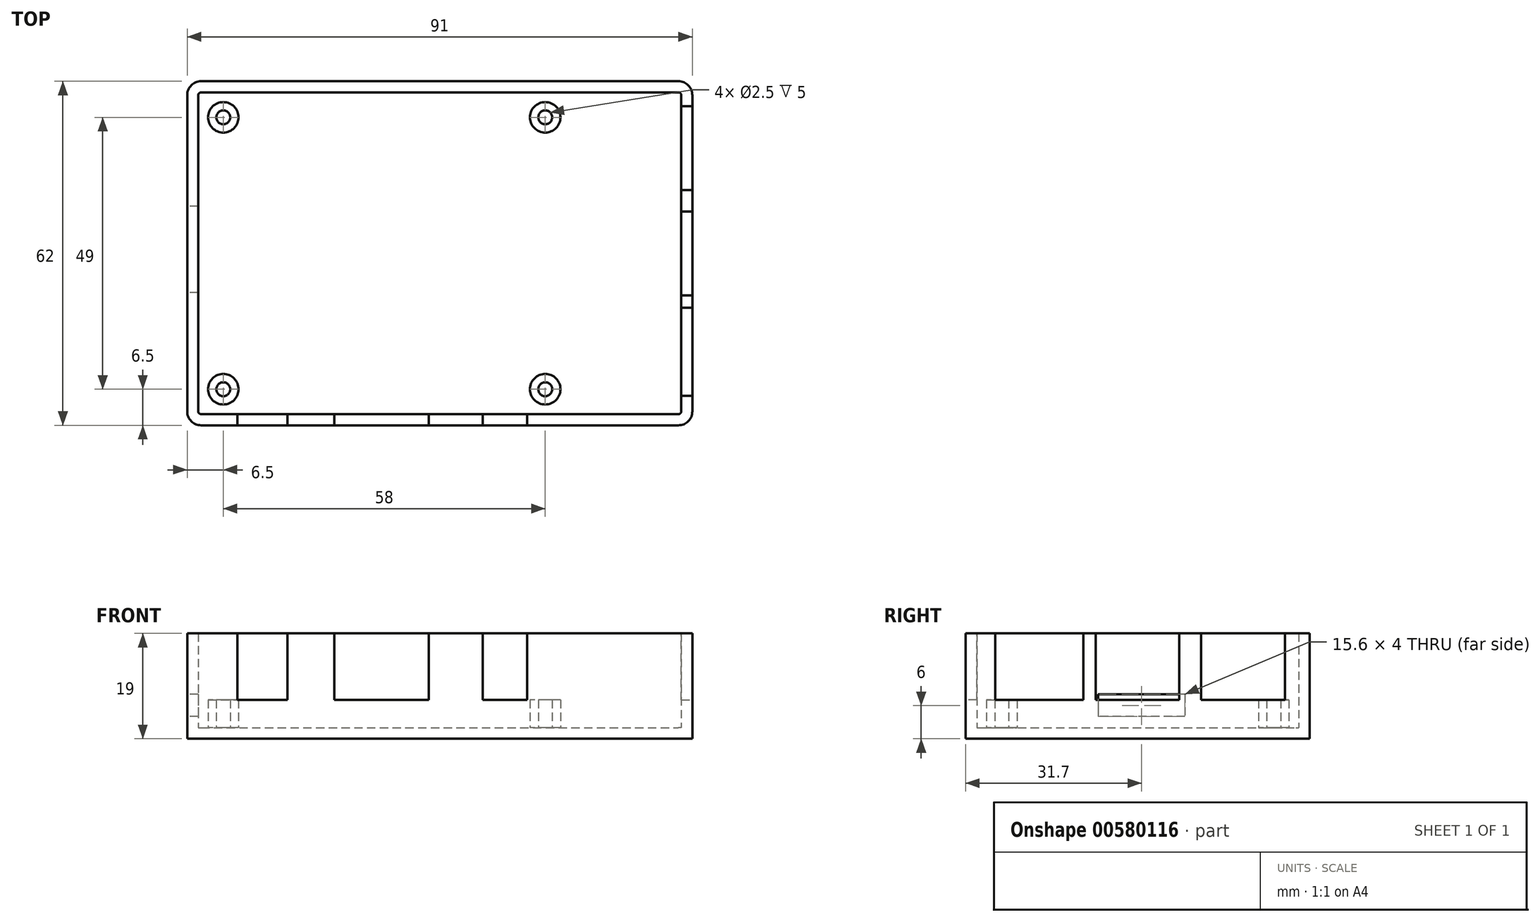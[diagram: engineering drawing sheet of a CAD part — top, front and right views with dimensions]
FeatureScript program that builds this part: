
annotation { "Feature Type Name" : "Feature", "Feature Type Description" : "" }
export const myFeature = defineFeature(function(context is Context, id is Id, definition is map)
    precondition{}
    {
        {
            var Q0;
            Q0=qCreatedBy(makeId("Top.planeOp"),FACE);
            var sketch = newSketch(context, id + "F0", { "sketchPlane" : qUnion([Q0])});
            skLineSegment(sketch, "E0.bottom", {"start": v(43, 31) * mm, "end": v(-43, 31) * mm});
            skLineSegment(sketch, "E0.top", {"start": v(43, -31) * mm, "end": v(-43, -31) * mm});
            skLineSegment(sketch, "E0.left", {"start": v(45.5, 28.5) * mm, "end": v(45.5, -28.5) * mm});
            skLineSegment(sketch, "E0.right", {"start": v(-45.5, 28.5) * mm, "end": v(-45.5, -28.5) * mm});
            skPoint(sketch, "E0.middle", {"position": v(0, 0) * mm});
            skPoint(sketch, "E1.visualSharp", {"position": v(-45.5, 31) * mm});
            skArc(sketch, "E1.filletArc", {"start": v(-43, 31) * mm, "mid": v(-44.77, 30.27) * mm, "end": v(-45.5, 28.5) * mm});
            skPoint(sketch, "E2.visualSharp", {"position": v(45.5, 31) * mm});
            skArc(sketch, "E2.filletArc", {"start": v(45.5, 28.5) * mm, "mid": v(44.77, 30.27) * mm, "end": v(43, 31) * mm});
            skPoint(sketch, "E3.visualSharp", {"position": v(45.5, -31) * mm});
            skArc(sketch, "E3.filletArc", {"start": v(43, -31) * mm, "mid": v(44.77, -30.27) * mm, "end": v(45.5, -28.5) * mm});
            skPoint(sketch, "E4.visualSharp", {"position": v(-45.5, -31) * mm});
            skArc(sketch, "E4.filletArc", {"start": v(-45.5, -28.5) * mm, "mid": v(-44.77, -30.27) * mm, "end": v(-43, -31) * mm});
            skArc(sketch, "E5.0", {"start": v(43.5, 28.5) * mm, "mid": v(43.35, 28.85) * mm, "end": v(43, 29) * mm});
            skLineSegment(sketch, "E5.1", {"start": v(43.5, 28.5) * mm, "end": v(43.5, -28.5) * mm});
            skLineSegment(sketch, "E5.2", {"start": v(43, 29) * mm, "end": v(-43, 29) * mm});
            skArc(sketch, "E5.3", {"start": v(43, -29) * mm, "mid": v(43.35, -28.85) * mm, "end": v(43.5, -28.5) * mm});
            skArc(sketch, "E5.4", {"start": v(-43, 29) * mm, "mid": v(-43.35, 28.85) * mm, "end": v(-43.5, 28.5) * mm});
            skLineSegment(sketch, "E5.5", {"start": v(-43.5, 28.5) * mm, "end": v(-43.5, -28.5) * mm});
            skArc(sketch, "E5.6", {"start": v(-43.5, -28.5) * mm, "mid": v(-43.35, -28.85) * mm, "end": v(-43, -29) * mm});
            skLineSegment(sketch, "E5.7", {"start": v(43, -29) * mm, "end": v(-43, -29) * mm});
            skSolve(sketch);
        }
        {
            var Q0;
            Q0=makeQuery(id+"F0.imprint","IMPRINT",FACE,{"disambiguationData":[TD([[makeQuery(id+"F0.imprint","IMPRINT",EDGE,{"derivedFrom":sQuery(id+"F0.wireOp",EDGE,"E0.bottom")}),1.0]])]});
            var Q1;
            Q1=makeQuery(id+"F0.imprint","IMPRINT",FACE,{"disambiguationData":[TD([[makeQuery(id+"F0.imprint","IMPRINT",EDGE,{"derivedFrom":sQuery(id+"F0.wireOp",EDGE,"E5.0")}),1.0]])]});
            extrude(context, id + "F1", {"entities" : qUnion([Q0, Q1]), "depth" : 2 * mm, "offsetDistance" : 25 * mm});
        }
        {
            var Q0;
            Q0 = qSketchRegion(id + "F0", true);
            extrude(context, id + "F2", {"entities" : qUnion([Q0]), "operationType" : NewBodyOperationType.ADD, "depth" : 19 * mm, "offsetDistance" : 25 * mm});
        }
        {
            var Q0;
            Q0=makeQuery(id+"F1.opExtrude","CAP_FACE",FACE,{"disambiguationData":[OSD([sQuery(id+"F0.wireOp",EDGE,"E0.bottom"),sQuery(id+"F0.wireOp",EDGE,"E0.top"),sQuery(id+"F0.wireOp",EDGE,"E0.left"),sQuery(id+"F0.wireOp",EDGE,"E0.right"),sQuery(id+"F0.wireOp",EDGE,"E1.filletArc"),sQuery(id+"F0.wireOp",EDGE,"E2.filletArc"),sQuery(id+"F0.wireOp",EDGE,"E3.filletArc"),sQuery(id+"F0.wireOp",EDGE,"E4.filletArc")])],"isStart":false});
            var sketch = newSketch(context, id + "F3", { "sketchPlane" : qUnion([Q0])});
            skCircle(sketch, "E6", {"center": v(-39, 24.5) * mm, "radius": 2.75 * mm});
            skCircle(sketch, "E7", {"center": v(19, 24.5) * mm, "radius": 2.75 * mm});
            skCircle(sketch, "E8", {"center": v(-39, -24.5) * mm, "radius": 2.75 * mm});
            skCircle(sketch, "E9", {"center": v(19, -24.5) * mm, "radius": 2.75 * mm});
            skCircle(sketch, "E10", {"center": v(-39, 24.5) * mm, "radius": 1.25 * mm});
            skCircle(sketch, "E11", {"center": v(19, 24.5) * mm, "radius": 1.25 * mm});
            skCircle(sketch, "E12", {"center": v(-39, -24.5) * mm, "radius": 1.25 * mm});
            skCircle(sketch, "E13", {"center": v(19, -24.5) * mm, "radius": 1.25 * mm});
            skSolve(sketch);
        }
        {
            var Q0;
            Q0 = qSketchRegion(id + "F3", true);
            extrude(context, id + "F4", {"entities" : qUnion([Q0]), "operationType" : NewBodyOperationType.ADD, "depth" : 5 * mm, "offsetDistance" : 25 * mm});
        }
        {
            var Q0;
            Q0=makeQuery(id+"F2.opExtrude","CAP_FACE",FACE,{"disambiguationData":[OSD([sQuery(id+"F0.wireOp",EDGE,"E0.bottom"),sQuery(id+"F0.wireOp",EDGE,"E0.top"),sQuery(id+"F0.wireOp",EDGE,"E0.left"),sQuery(id+"F0.wireOp",EDGE,"E0.right"),sQuery(id+"F0.wireOp",EDGE,"E1.filletArc"),sQuery(id+"F0.wireOp",EDGE,"E2.filletArc"),sQuery(id+"F0.wireOp",EDGE,"E3.filletArc"),sQuery(id+"F0.wireOp",EDGE,"E4.filletArc"),sQuery(id+"F0.wireOp",EDGE,"E5.0"),sQuery(id+"F0.wireOp",EDGE,"E5.1"),sQuery(id+"F0.wireOp",EDGE,"E5.2"),sQuery(id+"F0.wireOp",EDGE,"E5.3"),sQuery(id+"F0.wireOp",EDGE,"E5.4"),sQuery(id+"F0.wireOp",EDGE,"E5.5"),sQuery(id+"F0.wireOp",EDGE,"E5.6"),sQuery(id+"F0.wireOp",EDGE,"E5.7")])],"isStart":false});
            var sketch = newSketch(context, id + "F5", { "sketchPlane" : qUnion([Q0])});
            skLineSegment(sketch, "E14.top", {"start": v(-29.69, 29) * mm, "end": v(-34.69, 29) * mm});
            skLineSegment(sketch, "E15.top", {"start": v(-26.05, 29) * mm, "end": v(-21.05, 29) * mm});
            skLineSegment(sketch, "E16.top", {"start": v(-11.1, 29) * mm, "end": v(-15.76, 29) * mm});
            skLineSegment(sketch, "E17.bottom", {"start": v(-45.5, 16.08) * mm, "end": v(-43.5, 16.08) * mm});
            skLineSegment(sketch, "E17.left", {"start": v(-45.5, 16.08) * mm, "end": v(-45.5, 7.96) * mm});
            skLineSegment(sketch, "E17.right", {"start": v(-43.5, 16.08) * mm, "end": v(-43.5, 7.96) * mm});
            skLineSegment(sketch, "E18.left", {"start": v(-45.5, -0.46) * mm, "end": v(-45.5, -0.9) * mm});
            skLineSegment(sketch, "E18.right", {"start": v(-43.5, -0.46) * mm, "end": v(-43.5, -0.9) * mm});
            skLineSegment(sketch, "E19.left", {"start": v(-45.5, -16.53) * mm, "end": v(-45.5, -21.37) * mm});
            skLineSegment(sketch, "E19.right", {"start": v(-43.5, -16.53) * mm, "end": v(-43.5, -21.37) * mm});
            skLineSegment(sketch, "E20.bottom", {"start": v(43.5, 26.5) * mm, "end": v(45.5, 26.5) * mm});
            skLineSegment(sketch, "E20.top", {"start": v(43.5, 11.4) * mm, "end": v(45.5, 11.4) * mm});
            skLineSegment(sketch, "E20.left", {"start": v(43.5, 26.5) * mm, "end": v(43.5, 11.4) * mm});
            skLineSegment(sketch, "E20.right", {"start": v(45.5, 26.5) * mm, "end": v(45.5, 11.4) * mm});
            skLineSegment(sketch, "E21.bottom", {"start": v(43.5, 7.5) * mm, "end": v(45.5, 7.5) * mm});
            skLineSegment(sketch, "E21.top", {"start": v(43.5, -7.6) * mm, "end": v(45.5, -7.6) * mm});
            skLineSegment(sketch, "E21.left", {"start": v(43.5, 7.5) * mm, "end": v(43.5, -7.6) * mm});
            skLineSegment(sketch, "E21.right", {"start": v(45.5, 7.5) * mm, "end": v(45.5, -7.6) * mm});
            skLineSegment(sketch, "E22.bottom", {"start": v(43.5, -9.8) * mm, "end": v(45.5, -9.8) * mm});
            skLineSegment(sketch, "E22.top", {"start": v(43.5, -25.7) * mm, "end": v(45.5, -25.7) * mm});
            skLineSegment(sketch, "E22.left", {"start": v(43.5, -9.8) * mm, "end": v(43.5, -25.7) * mm});
            skLineSegment(sketch, "E22.right", {"start": v(45.5, -9.8) * mm, "end": v(45.5, -25.7) * mm});
            skLineSegment(sketch, "E23.bottom", {"start": v(-27.45, -31) * mm, "end": v(-36.45, -31) * mm});
            skLineSegment(sketch, "E23.top", {"start": v(-27.45, -29) * mm, "end": v(-36.45, -29) * mm});
            skLineSegment(sketch, "E23.left", {"start": v(-27.45, -31) * mm, "end": v(-27.45, -29) * mm});
            skLineSegment(sketch, "E23.right", {"start": v(-36.45, -31) * mm, "end": v(-36.45, -29) * mm});
            skLineSegment(sketch, "E24.bottom", {"start": v(-2, -29) * mm, "end": v(-19, -29) * mm});
            skLineSegment(sketch, "E24.top", {"start": v(-2, -31) * mm, "end": v(-19, -31) * mm});
            skLineSegment(sketch, "E24.left", {"start": v(-2, -29) * mm, "end": v(-2, -31) * mm});
            skLineSegment(sketch, "E24.right", {"start": v(-19, -29) * mm, "end": v(-19, -31) * mm});
            skLineSegment(sketch, "E25.bottom", {"start": v(15.75, -29) * mm, "end": v(7.75, -29) * mm});
            skLineSegment(sketch, "E25.top", {"start": v(15.75, -31) * mm, "end": v(7.75, -31) * mm});
            skLineSegment(sketch, "E25.left", {"start": v(15.75, -29) * mm, "end": v(15.75, -31) * mm});
            skLineSegment(sketch, "E25.right", {"start": v(7.75, -29) * mm, "end": v(7.75, -31) * mm});
            skSolve(sketch);
        }
        {
            var Q0;
            Q0=makeQuery(id+"F5.imprint","IMPRINT",FACE,{"disambiguationData":[TD([[makeQuery(id+"F5.imprint","IMPRINT",EDGE,{"derivedFrom":sQuery(id+"F5.wireOp",EDGE,"E23.bottom")}),-1.0]])]});
            var Q1;
            Q1=makeQuery(id+"F5.imprint","IMPRINT",FACE,{"disambiguationData":[TD([[makeQuery(id+"F5.imprint","IMPRINT",EDGE,{"derivedFrom":sQuery(id+"F5.wireOp",EDGE,"E24.bottom")}),1.0]])]});
            var Q2;
            Q2=makeQuery(id+"F5.imprint","IMPRINT",FACE,{"disambiguationData":[TD([[makeQuery(id+"F5.imprint","IMPRINT",EDGE,{"derivedFrom":sQuery(id+"F5.wireOp",EDGE,"E25.bottom")}),1.0]])]});
            var Q3;
            Q3=makeQuery(id+"F5.imprint","IMPRINT",FACE,{"disambiguationData":[TD([[makeQuery(id+"F5.imprint","IMPRINT",EDGE,{"derivedFrom":sQuery(id+"F5.wireOp",EDGE,"E22.bottom")}),-1.0]])]});
            var Q4;
            Q4=makeQuery(id+"F5.imprint","IMPRINT",FACE,{"disambiguationData":[TD([[makeQuery(id+"F5.imprint","IMPRINT",EDGE,{"derivedFrom":sQuery(id+"F5.wireOp",EDGE,"E21.bottom")}),-1.0]])]});
            var Q5;
            Q5=makeQuery(id+"F5.imprint","IMPRINT",FACE,{"disambiguationData":[TD([[makeQuery(id+"F5.imprint","IMPRINT",EDGE,{"derivedFrom":sQuery(id+"F5.wireOp",EDGE,"E20.bottom")}),-1.0]])]});
            extrude(context, id + "F6", {"entities" : qUnion([Q0, Q1, Q2, Q3, Q4, Q5]), "operationType" : NewBodyOperationType.REMOVE, "oppositeDirection" : true, "depth" : 12 * mm, "offsetDistance" : 25 * mm});
        }
        {
            var Q0;
            {var subQ0=sQuery(id+"F0.wireOp",EDGE,"E0.right");Q0=makeQuery(id+"F2.boolean.opBoolean","MERGE",FACE,{"derivedFrom":[makeQuery(id+"F1.opExtrude","SWEPT_FACE",FACE,{"disambiguationData":[OSD([subQ0])]}),makeQuery(id+"F2.opExtrude","SWEPT_FACE",FACE,{"disambiguationData":[OSD([subQ0])]})]});}
            var sketch = newSketch(context, id + "F7", { "sketchPlane" : qUnion([Q0])});
            skLineSegment(sketch, "E26.bottom", {"start": v(-8.5, 8) * mm, "end": v(7.1, 8) * mm});
            skLineSegment(sketch, "E26.top", {"start": v(-8.5, 4) * mm, "end": v(7.1, 4) * mm});
            skLineSegment(sketch, "E26.left", {"start": v(-8.5, 8) * mm, "end": v(-8.5, 4) * mm});
            skLineSegment(sketch, "E26.right", {"start": v(7.1, 8) * mm, "end": v(7.1, 4) * mm});
            skSolve(sketch);
        }
        {
            var Q0;
            Q0=makeQuery(id+"F7.imprint","IMPRINT",FACE,{"disambiguationData":[TD([[makeQuery(id+"F7.imprint","IMPRINT",EDGE,{"derivedFrom":sQuery(id+"F7.wireOp",EDGE,"E26.bottom")}),-1.0]])]});
            extrude(context, id + "F8", {"entities" : qUnion([Q0]), "operationType" : NewBodyOperationType.REMOVE, "endBound" : BoundingType.UP_TO_NEXT, "oppositeDirection" : true, "depth" : 25 * mm, "offsetDistance" : 25 * mm});
        }
    });
